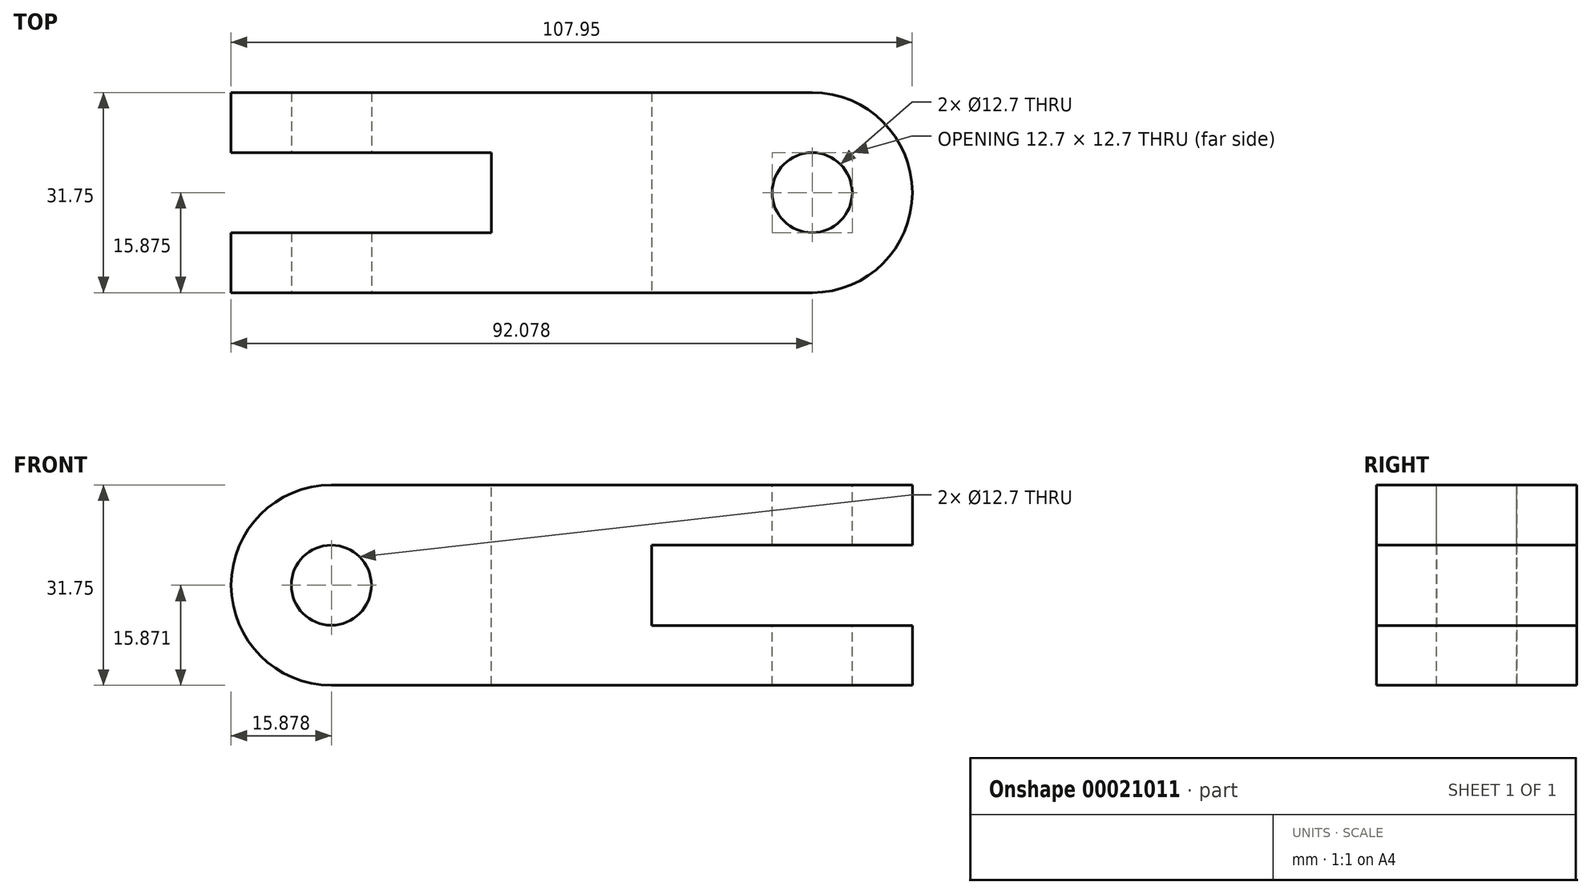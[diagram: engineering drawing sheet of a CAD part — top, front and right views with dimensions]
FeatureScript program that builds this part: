
annotation { "Feature Type Name" : "Feature", "Feature Type Description" : "" }
export const myFeature = defineFeature(function(context is Context, id is Id, definition is map)
    precondition{}
    {
        {
            var Q0;
            Q0=qCreatedBy(makeId("Front.planeOp"),FACE);
            var sketch = newSketch(context, id + "F0", { "sketchPlane" : qUnion([Q0])});
            skLineSegment(sketch, "E0.bottom", {"start": v(-103.56, 16.27) * mm, "end": v(4.4, 16.27) * mm});
            skLineSegment(sketch, "E0.top", {"start": v(-103.56, -15.48) * mm, "end": v(4.4, -15.48) * mm});
            skLineSegment(sketch, "E0.left", {"start": v(-103.56, 16.27) * mm, "end": v(-103.56, -15.48) * mm});
            skLineSegment(sketch, "E0.right", {"start": v(4.4, 16.27) * mm, "end": v(4.4, -15.48) * mm});
            skSolve(sketch);
        }
        {
            var Q0;
            Q0 = qSketchRegion(id + "F0", true);
            extrude(context, id + "F1", {"entities" : qUnion([Q0]), "depth" : 31.75 * mm});
        }
        {
            var Q0;
            Q0=makeQuery(id+"F1.opExtrude","CAP_FACE",FACE,{"disambiguationData":[OSD([sQuery(id+"F0.wireOp",EDGE,"E0.bottom"),sQuery(id+"F0.wireOp",EDGE,"E0.top"),sQuery(id+"F0.wireOp",EDGE,"E0.left"),sQuery(id+"F0.wireOp",EDGE,"E0.right")])],"isStart":false});
            var sketch = newSketch(context, id + "F2", { "sketchPlane" : qUnion([Q0])});
            skArc(sketch, "E1", {"start": v(-87.68, 16.27) * mm, "mid": v(-103.56, 0.4) * mm, "end": v(-87.68, -15.48) * mm});
            skCircle(sketch, "E2", {"center": v(-87.68, 0.4) * mm, "radius": 6.35 * mm});
            skLineSegment(sketch, "E3.0", {"start": v(-36.88, 6.74) * mm, "end": v(-36.88, -6) * mm});
            skLineSegment(sketch, "E4.trimOffspring", {"start": v(-36.88, 6.74) * mm, "end": v(4.4, 6.74) * mm});
            skLineSegment(sketch, "E5.trimOffspring", {"start": v(-36.88, -6) * mm, "end": v(4.4, -6) * mm});
            skSolve(sketch);
        }
        {
            var Q0;
            {var subQ1=sQuery(id+"F2.wireOp",EDGE,"E1");var subQ3=makeQuery(id+"F1.opExtrude","CAP_EDGE",EDGE,{"disambiguationData":[OSD([sQuery(id+"F0.wireOp",EDGE,"E0.bottom")])],"isStart":false});var subQ5=makeQuery(id+"F2.imprint","INTERSECT",VERTEX,{"derivedFrom":[subQ3,subQ1]});Q0=makeQuery(id+"F2.imprint","IMPRINT",FACE,{"disambiguationData":[TD([[makeQuery(id+"F2.imprint","IMPRINT",EDGE,{"disambiguationData":[TD([[subQ5,-1.0]])],"derivedFrom":subQ1}),-1.0]])]});}
            var Q1;
            {var subQ1=sQuery(id+"F2.wireOp",EDGE,"E1");var subQ3=makeQuery(id+"F1.opExtrude","CAP_EDGE",EDGE,{"disambiguationData":[OSD([sQuery(id+"F0.wireOp",EDGE,"E0.top")])],"isStart":false});var subQ5=makeQuery(id+"F2.imprint","INTERSECT",VERTEX,{"derivedFrom":[subQ3,subQ1]});Q1=makeQuery(id+"F2.imprint","IMPRINT",FACE,{"disambiguationData":[TD([[makeQuery(id+"F2.imprint","IMPRINT",EDGE,{"disambiguationData":[TD([[subQ5,1.0]])],"derivedFrom":subQ1}),-1.0]])]});}
            var Q2;
            Q2=makeQuery(id+"F2.imprint","IMPRINT",FACE,{"disambiguationData":[TD([[makeQuery(id+"F2.imprint","IMPRINT",EDGE,{"derivedFrom":sQuery(id+"F2.wireOp",EDGE,"E2")}),1.0]])]});
            var Q3;
            Q3=makeQuery(id+"F2.imprint","IMPRINT",FACE,{"disambiguationData":[TD([[makeQuery(id+"F2.imprint","IMPRINT",EDGE,{"derivedFrom":sQuery(id+"F2.wireOp",EDGE,"E3.0")}),1.0]])]});
            extrude(context, id + "F3", {"entities" : qUnion([Q0, Q1, Q2, Q3]), "operationType" : NewBodyOperationType.REMOVE, "oppositeDirection" : true, "depth" : 304.8 * mm});
        }
        {
            var Q0;
            Q0=makeQuery(id+"F1.opExtrude","SWEPT_FACE",FACE,{"disambiguationData":[OSD([sQuery(id+"F0.wireOp",EDGE,"E0.bottom")])]});
            var sketch = newSketch(context, id + "F4", { "sketchPlane" : qUnion([Q0])});
            skLineSegment(sketch, "E6", {"start": v(-103.56, 0) * mm, "end": v(4.4, 0) * mm});
            skLineSegment(sketch, "E7", {"start": v(4.4, 0) * mm, "end": v(4.4, -31.75) * mm});
            skLineSegment(sketch, "E8", {"start": v(4.4, -31.75) * mm, "end": v(-103.56, -31.75) * mm});
            skLineSegment(sketch, "E9", {"start": v(-103.56, -31.75) * mm, "end": v(-103.56, 0) * mm});
            skLineSegment(sketch, "E10.0", {"start": v(-11.48, -9.52) * mm, "end": v(-11.48, -22.23) * mm});
            skArc(sketch, "E11", {"start": v(-11.48, -31.75) * mm, "mid": v(4.4, -15.88) * mm, "end": v(-11.48, 0) * mm});
            skCircle(sketch, "E12", {"center": v(-11.48, -15.88) * mm, "radius": 6.35 * mm});
            skLineSegment(sketch, "E13.0", {"start": v(-103.56, -9.53) * mm, "end": v(-62.28, -9.53) * mm});
            skLineSegment(sketch, "E14.0", {"start": v(-62.28, -22.23) * mm, "end": v(-62.28, -9.52) * mm});
            skLineSegment(sketch, "E15.trimOffspring", {"start": v(-62.28, -22.23) * mm, "end": v(-103.56, -22.23) * mm});
            skSolve(sketch);
        }
        {
            var Q0;
            {var subQ5=sQuery(id+"F4.wireOp",EDGE,"E14.0");Q0=makeQuery(id+"F4.imprint","IMPRINT",FACE,{"disambiguationData":[TD([[makeQuery(id+"F4.imprint","IMPRINT",EDGE,{"derivedFrom":subQ5}),1.0]])]});}
            var Q1;
            {var subQ3=sQuery(id+"F4.wireOp",EDGE,"E9");var subQ5=sQuery(id+"F4.wireOp",EDGE,"E13.0");var subQ7=makeQuery(id+"F4.imprint","INTERSECT",VERTEX,{"derivedFrom":[subQ3,subQ5]});Q1=makeQuery(id+"F4.imprint","IMPRINT",FACE,{"disambiguationData":[TD([[makeQuery(id+"F4.imprint","IMPRINT",EDGE,{"disambiguationData":[TD([[subQ7,1.0]])],"derivedFrom":subQ3}),-1.0]])]});}
            var Q2;
            {var subQ1=sQuery(id+"F4.wireOp",EDGE,"E7");var subQ3=sQuery(id+"F4.wireOp",EDGE,"E6");var subQ5=makeQuery(id+"F4.imprint","INTERSECT",VERTEX,{"derivedFrom":[subQ3,subQ1]});Q2=makeQuery(id+"F4.imprint","IMPRINT",FACE,{"disambiguationData":[TD([[makeQuery(id+"F4.imprint","IMPRINT",EDGE,{"disambiguationData":[TD([[subQ5,1.0]])],"derivedFrom":subQ3}),-1.0]])]});}
            var Q3;
            {var subQ1=sQuery(id+"F4.wireOp",EDGE,"E7");var subQ3=sQuery(id+"F4.wireOp",EDGE,"E8");var subQ5=makeQuery(id+"F4.imprint","INTERSECT",VERTEX,{"derivedFrom":[subQ1,subQ3]});Q3=makeQuery(id+"F4.imprint","IMPRINT",FACE,{"disambiguationData":[TD([[makeQuery(id+"F4.imprint","IMPRINT",EDGE,{"disambiguationData":[TD([[subQ5,-1.0]])],"derivedFrom":subQ1}),1.0]])]});}
            var Q4;
            {var subQ1=sQuery(id+"F4.wireOp",EDGE,"E10.0");Q4=makeQuery(id+"F4.imprint","IMPRINT",FACE,{"disambiguationData":[TD([[makeQuery(id+"F4.imprint","IMPRINT",EDGE,{"derivedFrom":subQ1}),-1.0]])]});}
            var Q5;
            {var subQ1=sQuery(id+"F4.wireOp",EDGE,"E10.0");Q5=makeQuery(id+"F4.imprint","IMPRINT",FACE,{"disambiguationData":[TD([[makeQuery(id+"F4.imprint","IMPRINT",EDGE,{"derivedFrom":subQ1}),1.0]])]});}
            extrude(context, id + "F5", {"entities" : qUnion([Q0, Q1, Q2, Q3, Q4, Q5]), "operationType" : NewBodyOperationType.REMOVE, "endBound" : BoundingType.THROUGH_ALL, "oppositeDirection" : true, "depth" : 25.4 * mm});
        }
        {
            var Q0;
            Q0=makeQuery(id+"F1.opExtrude","SWEPT_BODY",BODY,{"disambiguationData":[OSD([sQuery(id+"F0.wireOp",EDGE,"E0.bottom"),sQuery(id+"F0.wireOp",EDGE,"E0.top"),sQuery(id+"F0.wireOp",EDGE,"E0.left"),sQuery(id+"F0.wireOp",EDGE,"E0.right")])]});
            transform(context, id + "F6", {"entities" : qUnion([Q0]), "transformType" : TransformType.TRANSLATION_3D, "dx" : 0 * mm, "dy" : 0 * mm, "dz" : 0 * mm, "makeCopy" : true});
        }
        {
            var Q0;
            Q0=makeQuery(id+"F6.opPattern","COPY",BODY,{"derivedFrom":makeQuery(id+"F1.opExtrude","SWEPT_BODY",BODY,{"disambiguationData":[OSD([sQuery(id+"F0.wireOp",EDGE,"E0.bottom"),sQuery(id+"F0.wireOp",EDGE,"E0.top"),sQuery(id+"F0.wireOp",EDGE,"E0.left"),sQuery(id+"F0.wireOp",EDGE,"E0.right")])]}),"instanceName":"1"});
            deleteBodies(context, id + "F7", {"entities" : qUnion([Q0])});
        }
    });
